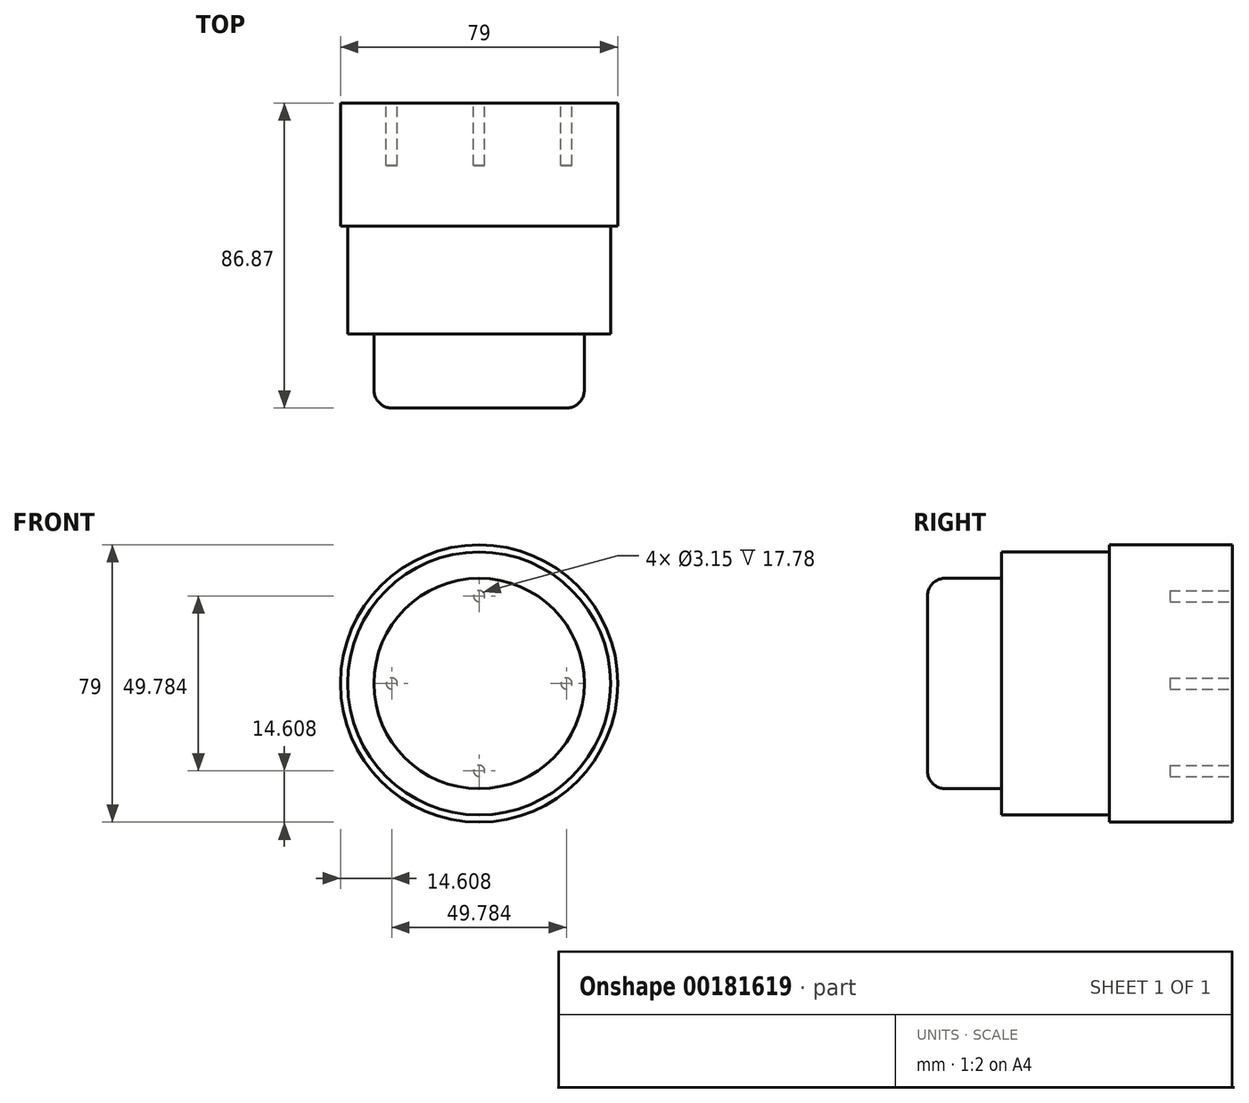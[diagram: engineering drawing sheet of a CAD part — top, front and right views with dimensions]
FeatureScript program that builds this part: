
annotation { "Feature Type Name" : "Feature", "Feature Type Description" : "" }
export const myFeature = defineFeature(function(context is Context, id is Id, definition is map)
    precondition{}
    {
        {
            var Q0;
            Q0=qCreatedBy(makeId("Front.planeOp"),FACE);
            var sketch = newSketch(context, id + "F0", { "sketchPlane" : qUnion([Q0])});
            skCircle(sketch, "E0", {"center": v(0, 0) * mm, "radius": 39.5 * mm});
            skSolve(sketch);
        }
        {
            var Q0;
            Q0 = qSketchRegion(id + "F0", true);
            extrude(context, id + "F1", {"entities" : qUnion([Q0]), "depth" : 91.19 * mm});
        }
        {
            var Q0;
            Q0=makeQuery(id+"F1.opExtrude","CAP_FACE",FACE,{"disambiguationData":[OSD([sQuery(id+"F0.wireOp",EDGE,"E0")])],"isStart":false});
            var sketch = newSketch(context, id + "F2", { "sketchPlane" : qUnion([Q0])});
            skCircle(sketch, "E1", {"center": v(0, 0) * mm, "radius": 37.47 * mm});
            skCircle(sketch, "E2", {"center": v(0, 0) * mm, "radius": 39.57 * mm});
            skSolve(sketch);
        }
        {
            var Q0;
            Q0=makeQuery(id+"F2.imprint","IMPRINT",FACE,{"disambiguationData":[TD([[makeQuery(id+"F2.imprint","IMPRINT",EDGE,{"derivedFrom":sQuery(id+"F2.wireOp",EDGE,"E1")}),-1.0]])]});
            extrude(context, id + "F3", {"entities" : qUnion([Q0]), "operationType" : NewBodyOperationType.REMOVE, "oppositeDirection" : true, "depth" : 56.13 * mm});
        }
        {
            var Q0;
            Q0=makeQuery(id+"F1.opExtrude","CAP_FACE",FACE,{"disambiguationData":[OSD([sQuery(id+"F0.wireOp",EDGE,"E0")])],"isStart":false});
            var sketch = newSketch(context, id + "F4", { "sketchPlane" : qUnion([Q0])});
            skCircle(sketch, "E3", {"center": v(0, 0) * mm, "radius": 32.9 * mm});
            skSolve(sketch);
        }
        {
            var Q0;
            Q0 = qSketchRegion(id + "F4", true);
            var Q1;
            Q1=makeQuery(id+"F4.imprint","IMPRINT",FACE,{"disambiguationData":[TD([[makeQuery(id+"F4.imprint","IMPRINT",EDGE,{"derivedFrom":sQuery(id+"F4.wireOp",EDGE,"E3")}),-1.0]])]});
            extrude(context, id + "F5", {"entities" : qUnion([Q0, Q1]), "operationType" : NewBodyOperationType.REMOVE, "oppositeDirection" : true, "depth" : 25.4 * mm});
        }
        {
            var Q0;
            Q0=makeQuery(id+"F5.boolean.opBoolean","COPY",FACE,{"derivedFrom":makeQuery(id+"F5.opExtrude","CAP_FACE",FACE,{"disambiguationData":[OSD([sQuery(id+"F2.wireOp",EDGE,"E1")])],"isStart":false})});
            var sketch = newSketch(context, id + "F6", { "sketchPlane" : qUnion([Q0])});
            skCircle(sketch, "E4", {"center": v(0, 0) * mm, "radius": 29.97 * mm});
            skSolve(sketch);
        }
        {
            var Q0;
            Q0 = qSketchRegion(id + "F6", true);
            extrude(context, id + "F7", {"entities" : qUnion([Q0]), "operationType" : NewBodyOperationType.ADD, "depth" : 21.08 * mm});
        }
        {
            var Q0;
            Q0=makeQuery(id+"F1.opExtrude","CAP_FACE",FACE,{"disambiguationData":[OSD([sQuery(id+"F0.wireOp",EDGE,"E0")])],"isStart":true});
            var sketch = newSketch(context, id + "F8", { "sketchPlane" : qUnion([Q0])});
            skLineSegment(sketch, "E5", {"start": v(0, 39.5) * mm, "end": v(0, 26.47) * mm});
            skLineSegment(sketch, "E6", {"start": v(-39.5, 0) * mm, "end": v(-26.47, 0) * mm});
            skCircle(sketch, "E7", {"center": v(0, 24.9) * mm, "radius": 1.57 * mm});
            skCircle(sketch, "E8", {"center": v(24.9, 0) * mm, "radius": 1.57 * mm});
            skCircle(sketch, "E9", {"center": v(0, -24.9) * mm, "radius": 1.57 * mm});
            skCircle(sketch, "E10.MirrorC", {"center": v(-24.9, 0) * mm, "radius": 1.57 * mm});
            skLineSegment(sketch, "E11.trimOffspring", {"start": v(-23.32, 0) * mm, "end": v(23.32, 0) * mm});
            skLineSegment(sketch, "E12.trimOffspring", {"start": v(0, 23.32) * mm, "end": v(0, -23.32) * mm});
            skLineSegment(sketch, "E13.trimOffspring", {"start": v(26.47, 0) * mm, "end": v(39.5, 0) * mm});
            skLineSegment(sketch, "E14.trimOffspring", {"start": v(0, -26.47) * mm, "end": v(0, -39.5) * mm});
            skSolve(sketch);
        }
        {
            var Q0;
            Q0 = qSketchRegion(id + "F8", true);
            extrude(context, id + "F9", {"entities" : qUnion([Q0]), "operationType" : NewBodyOperationType.REMOVE, "oppositeDirection" : true, "depth" : 17.78 * mm});
        }
        {
            var Q0;
            Q0=makeQuery(id+"F5.boolean.opBoolean","COPY",EDGE,{"derivedFrom":makeQuery(id+"F5.opExtrude","CAP_EDGE",EDGE,{"disambiguationData":[OSD([sQuery(id+"F2.wireOp",EDGE,"E1")])],"isStart":false})});
            var Q1;
            Q1=makeQuery(id+"F3.boolean.opBoolean","COPY",EDGE,{"derivedFrom":makeQuery(id+"F3.opExtrude","CAP_EDGE",EDGE,{"disambiguationData":[OSD([sQuery(id+"F0.wireOp",EDGE,"E0")])],"isStart":false})});
            var Q2;
            Q2=makeQuery(id+"F7.opExtrude","CAP_EDGE",EDGE,{"disambiguationData":[OSD([sQuery(id+"F6.wireOp",EDGE,"E4")])],"isStart":false});
            fillet(context, id + "F10", {"entities" : qUnion([Q0, Q1, Q2]), "radius" : 5.08 * mm, "tangentPropagation" : true, "allowEdgeOverflow" : false});
        }
    });
